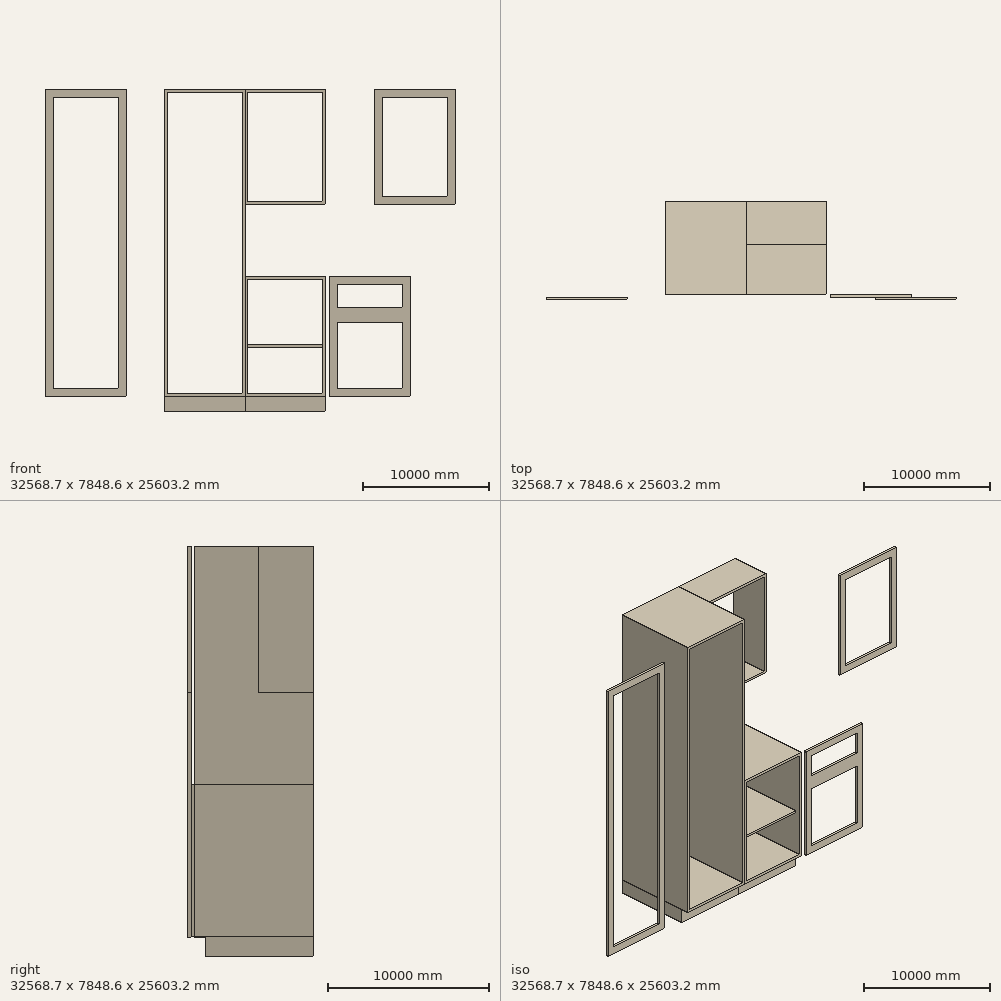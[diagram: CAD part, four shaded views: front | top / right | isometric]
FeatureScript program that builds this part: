
annotation { "Feature Type Name" : "Feature", "Feature Type Description" : "" }
export const myFeature = defineFeature(function(context is Context, id is Id, definition is map)
    precondition{}
    {
        {
            var Q0;
            Q0=qCreatedBy(makeId("Front.planeOp"),FACE);
            var sketch = newSketch(context, id + "F0", { "sketchPlane" : qUnion([Q0])});
            skLineSegment(sketch, "E0.bottom", {"start": v(0, 0) * mm, "end": v(6400.8, 0) * mm});
            skLineSegment(sketch, "E0.top", {"start": v(0, 24384) * mm, "end": v(6400.8, 24384) * mm});
            skLineSegment(sketch, "E0.left", {"start": v(0, 0) * mm, "end": v(0, 24384) * mm});
            skLineSegment(sketch, "E0.right", {"start": v(6400.8, 0) * mm, "end": v(6400.8, 24384) * mm});
            skSolve(sketch);
        }
        {
            var Q0;
            Q0=qCreatedBy(makeId("Front.planeOp"),FACE);
            var sketch = newSketch(context, id + "F1", { "sketchPlane" : qUnion([Q0])});
            skLineSegment(sketch, "E1.bottom", {"start": v(6400.8, 0) * mm, "end": v(12801.6, 0) * mm});
            skLineSegment(sketch, "E1.top", {"start": v(6400.8, 9525) * mm, "end": v(12801.6, 9525) * mm});
            skLineSegment(sketch, "E1.left", {"start": v(6400.8, 0) * mm, "end": v(6400.8, 9525) * mm});
            skLineSegment(sketch, "E1.right", {"start": v(12801.6, 0) * mm, "end": v(12801.6, 9525) * mm});
            skSolve(sketch);
        }
        {
            var Q0;
            Q0=qCreatedBy(makeId("Front.planeOp"),FACE);
            var sketch = newSketch(context, id + "F2", { "sketchPlane" : qUnion([Q0])});
            skLineSegment(sketch, "E2.bottom", {"start": v(6400.8, 24384) * mm, "end": v(12801.6, 24384) * mm});
            skLineSegment(sketch, "E2.top", {"start": v(6400.8, 15240) * mm, "end": v(12801.6, 15240) * mm});
            skLineSegment(sketch, "E2.left", {"start": v(6400.8, 24384) * mm, "end": v(6400.8, 15240) * mm});
            skLineSegment(sketch, "E2.right", {"start": v(12801.6, 24384) * mm, "end": v(12801.6, 15240) * mm});
            skSolve(sketch);
        }
        {
            var Q0;
            Q0=makeQuery(id+"F0.imprint","IMPRINT",FACE,{"disambiguationData":[TD([[makeQuery(id+"F0.imprint","IMPRINT",EDGE,{"derivedFrom":sQuery(id+"F0.wireOp",EDGE,"E0.bottom")}),1.0]])]});
            extrude(context, id + "F3", {"entities" : qUnion([Q0]), "depth" : 7391.4 * mm});
        }
        {
            var Q0;
            Q0=makeQuery(id+"F2.imprint","IMPRINT",FACE,{"disambiguationData":[TD([[makeQuery(id+"F2.imprint","IMPRINT",EDGE,{"derivedFrom":sQuery(id+"F2.wireOp",EDGE,"E2.bottom")}),-1.0]])]});
            extrude(context, id + "F4", {"entities" : qUnion([Q0]), "depth" : 3429 * mm});
        }
        {
            var Q0;
            Q0=makeQuery(id+"F1.imprint","IMPRINT",FACE,{"disambiguationData":[TD([[makeQuery(id+"F1.imprint","IMPRINT",EDGE,{"derivedFrom":sQuery(id+"F1.wireOp",EDGE,"E1.bottom")}),1.0]])]});
            extrude(context, id + "F5", {"entities" : qUnion([Q0]), "depth" : 7391.4 * mm});
        }
        {
            var Q0;
            Q0=qCreatedBy(makeId("Front.planeOp"),FACE);
            var sketch = newSketch(context, id + "F6", { "sketchPlane" : qUnion([Q0])});
            skLineSegment(sketch, "E3.bottom", {"start": v(0, 0) * mm, "end": v(6400.8, 0) * mm});
            skLineSegment(sketch, "E3.top", {"start": v(0, -1219.2) * mm, "end": v(6400.8, -1219.2) * mm});
            skLineSegment(sketch, "E3.left", {"start": v(0, 0) * mm, "end": v(0, -1219.2) * mm});
            skLineSegment(sketch, "E3.right", {"start": v(6400.8, 0) * mm, "end": v(6400.8, -1219.2) * mm});
            skSolve(sketch);
        }
        {
            var Q0;
            Q0=makeQuery(id+"F6.imprint","IMPRINT",FACE,{"disambiguationData":[TD([[makeQuery(id+"F6.imprint","IMPRINT",EDGE,{"derivedFrom":sQuery(id+"F6.wireOp",EDGE,"E3.bottom")}),-1.0]])]});
            var sketch = newSketch(context, id + "F7", { "sketchPlane" : qUnion([Q0])});
            skLineSegment(sketch, "E4.bottom", {"start": v(6400.8, -1219.2) * mm, "end": v(12801.6, -1219.2) * mm});
            skLineSegment(sketch, "E4.top", {"start": v(6400.8, 0) * mm, "end": v(12801.6, 0) * mm});
            skLineSegment(sketch, "E4.left", {"start": v(6400.8, -1219.2) * mm, "end": v(6400.8, 0) * mm});
            skLineSegment(sketch, "E4.right", {"start": v(12801.6, -1219.2) * mm, "end": v(12801.6, 0) * mm});
            skSolve(sketch);
        }
        {
            var Q0;
            Q0=makeQuery(id+"F6.imprint","IMPRINT",FACE,{"disambiguationData":[TD([[makeQuery(id+"F6.imprint","IMPRINT",EDGE,{"derivedFrom":sQuery(id+"F6.wireOp",EDGE,"E3.bottom")}),-1.0]])]});
            extrude(context, id + "F8", {"entities" : qUnion([Q0]), "depth" : 6705.6 * mm});
        }
        {
            var Q0;
            Q0=makeQuery(id+"F7.imprint","IMPRINT",FACE,{"disambiguationData":[TD([[makeQuery(id+"F7.imprint","IMPRINT",EDGE,{"derivedFrom":sQuery(id+"F7.wireOp",EDGE,"E4.bottom")}),1.0]])]});
            extrude(context, id + "F9", {"entities" : qUnion([Q0]), "depth" : 6705.6 * mm});
        }
        {
            var Q0;
            Q0=makeQuery(id+"F3.opExtrude","CAP_FACE",FACE,{"disambiguationData":[OSD([sQuery(id+"F0.wireOp",EDGE,"E0.bottom"),sQuery(id+"F0.wireOp",EDGE,"E0.top"),sQuery(id+"F0.wireOp",EDGE,"E0.left"),sQuery(id+"F0.wireOp",EDGE,"E0.right")])],"isStart":false});
            var sketch = newSketch(context, id + "F10", { "sketchPlane" : qUnion([Q0])});
            skLineSegment(sketch, "E5.bottom", {"start": v(609.6, 23774.4) * mm, "end": v(5791.2, 23774.4) * mm});
            skLineSegment(sketch, "E5.top", {"start": v(609.6, 609.6) * mm, "end": v(5791.2, 609.6) * mm});
            skLineSegment(sketch, "E5.left", {"start": v(609.6, 23774.4) * mm, "end": v(609.6, 609.6) * mm});
            skLineSegment(sketch, "E5.right", {"start": v(5791.2, 23774.4) * mm, "end": v(5791.2, 609.6) * mm});
            skSolve(sketch);
        }
        {
            var Q0;
            Q0=makeQuery(id+"F3.opExtrude","CAP_FACE",FACE,{"disambiguationData":[OSD([sQuery(id+"F0.wireOp",EDGE,"E0.bottom"),sQuery(id+"F0.wireOp",EDGE,"E0.top"),sQuery(id+"F0.wireOp",EDGE,"E0.left"),sQuery(id+"F0.wireOp",EDGE,"E0.right")])],"isStart":true});
            var sketch = newSketch(context, id + "F11", { "sketchPlane" : qUnion([Q0])});
            skLineSegment(sketch, "E6.bottom", {"start": v(-6172.2, 24155.4) * mm, "end": v(-228.6, 24155.4) * mm});
            skLineSegment(sketch, "E6.top", {"start": v(-6172.2, 228.6) * mm, "end": v(-228.6, 228.6) * mm});
            skLineSegment(sketch, "E6.left", {"start": v(-6172.2, 24155.4) * mm, "end": v(-6172.2, 228.6) * mm});
            skLineSegment(sketch, "E6.right", {"start": v(-228.6, 24155.4) * mm, "end": v(-228.6, 228.6) * mm});
            skSolve(sketch);
        }
        {
            var Q0;
            Q0=makeQuery(id+"F11.imprint","IMPRINT",FACE,{"disambiguationData":[TD([[makeQuery(id+"F11.imprint","IMPRINT",EDGE,{"derivedFrom":sQuery(id+"F11.wireOp",EDGE,"E6.bottom")}),-1.0]])]});
            extrude(context, id + "F12", {"entities" : qUnion([Q0]), "operationType" : NewBodyOperationType.REMOVE, "oppositeDirection" : true, "depth" : 7391.4 * mm});
        }
        {
            var Q0;
            Q0 = qSketchRegion(id + "F10", true);
            extrude(context, id + "F13", {"entities" : qUnion([Q0]), "operationType" : NewBodyOperationType.REMOVE, "depth" : 228.6 * mm});
        }
        {
            var Q0;
            Q0=makeQuery(id+"F3.opExtrude","CAP_FACE",FACE,{"disambiguationData":[OSD([sQuery(id+"F0.wireOp",EDGE,"E0.bottom"),sQuery(id+"F0.wireOp",EDGE,"E0.top"),sQuery(id+"F0.wireOp",EDGE,"E0.left"),sQuery(id+"F0.wireOp",EDGE,"E0.right")])],"isStart":false});
            var sketch = newSketch(context, id + "F14", { "sketchPlane" : qUnion([Q0])});
            skLineSegment(sketch, "E7.bottom", {"start": v(0, 0) * mm, "end": v(6400.8, 0) * mm});
            skLineSegment(sketch, "E7.top", {"start": v(0, 24384) * mm, "end": v(6400.8, 24384) * mm});
            skLineSegment(sketch, "E7.left", {"start": v(0, 0) * mm, "end": v(0, 24384) * mm});
            skLineSegment(sketch, "E7.right", {"start": v(6400.8, 0) * mm, "end": v(6400.8, 24384) * mm});
            skSolve(sketch);
        }
        {
            var Q0;
            Q0=makeQuery(id+"F4.opExtrude","CAP_FACE",FACE,{"disambiguationData":[OSD([sQuery(id+"F2.wireOp",EDGE,"E2.bottom"),sQuery(id+"F2.wireOp",EDGE,"E2.top"),sQuery(id+"F2.wireOp",EDGE,"E2.left"),sQuery(id+"F2.wireOp",EDGE,"E2.right")])],"isStart":true});
            var sketch = newSketch(context, id + "F15", { "sketchPlane" : qUnion([Q0])});
            skLineSegment(sketch, "E8.bottom", {"start": v(-12573, 24155.4) * mm, "end": v(-6629.4, 24155.4) * mm});
            skLineSegment(sketch, "E8.top", {"start": v(-12573, 15468.6) * mm, "end": v(-6629.4, 15468.6) * mm});
            skLineSegment(sketch, "E8.left", {"start": v(-12573, 24155.4) * mm, "end": v(-12573, 15468.6) * mm});
            skLineSegment(sketch, "E8.right", {"start": v(-6629.4, 24155.4) * mm, "end": v(-6629.4, 15468.6) * mm});
            skSolve(sketch);
        }
        {
            var Q0;
            Q0=makeQuery(id+"F15.imprint","IMPRINT",FACE,{"disambiguationData":[TD([[makeQuery(id+"F15.imprint","IMPRINT",EDGE,{"derivedFrom":sQuery(id+"F15.wireOp",EDGE,"E8.bottom")}),-1.0]])]});
            extrude(context, id + "F16", {"entities" : qUnion([Q0]), "operationType" : NewBodyOperationType.REMOVE, "oppositeDirection" : true, "depth" : 3429 * mm});
        }
        {
            var Q0;
            Q0=makeQuery(id+"F5.opExtrude","CAP_FACE",FACE,{"disambiguationData":[OSD([sQuery(id+"F1.wireOp",EDGE,"E1.bottom"),sQuery(id+"F1.wireOp",EDGE,"E1.top"),sQuery(id+"F1.wireOp",EDGE,"E1.left"),sQuery(id+"F1.wireOp",EDGE,"E1.right")])],"isStart":true});
            var sketch = newSketch(context, id + "F17", { "sketchPlane" : qUnion([Q0])});
            skLineSegment(sketch, "E9.bottom", {"start": v(-12573, 228.6) * mm, "end": v(-6629.4, 228.6) * mm});
            skLineSegment(sketch, "E9.top", {"start": v(-12573, 9296.4) * mm, "end": v(-6629.4, 9296.4) * mm});
            skLineSegment(sketch, "E9.left", {"start": v(-12573, 228.6) * mm, "end": v(-12573, 9296.4) * mm});
            skLineSegment(sketch, "E9.right", {"start": v(-6629.4, 228.6) * mm, "end": v(-6629.4, 9296.4) * mm});
            skSolve(sketch);
        }
        {
            var Q0;
            Q0=makeQuery(id+"F17.imprint","IMPRINT",FACE,{"disambiguationData":[TD([[makeQuery(id+"F17.imprint","IMPRINT",EDGE,{"derivedFrom":sQuery(id+"F17.wireOp",EDGE,"E9.bottom")}),1.0]])]});
            extrude(context, id + "F18", {"entities" : qUnion([Q0]), "operationType" : NewBodyOperationType.REMOVE, "oppositeDirection" : true, "depth" : 7391.4 * mm});
        }
        {
            var Q0;
            Q0=makeQuery(id+"F5.opExtrude","CAP_FACE",FACE,{"disambiguationData":[OSD([sQuery(id+"F1.wireOp",EDGE,"E1.bottom"),sQuery(id+"F1.wireOp",EDGE,"E1.top"),sQuery(id+"F1.wireOp",EDGE,"E1.left"),sQuery(id+"F1.wireOp",EDGE,"E1.right")])],"isStart":false});
            var sketch = newSketch(context, id + "F19", { "sketchPlane" : qUnion([Q0])});
            skLineSegment(sketch, "E10.bottom", {"start": v(13107.73, 9525) * mm, "end": v(19508.53, 9525) * mm});
            skLineSegment(sketch, "E10.top", {"start": v(13107.73, 0) * mm, "end": v(19508.53, 0) * mm});
            skLineSegment(sketch, "E10.left", {"start": v(13107.73, 9525) * mm, "end": v(13107.73, 0) * mm});
            skLineSegment(sketch, "E10.right", {"start": v(19508.53, 9525) * mm, "end": v(19508.53, 0) * mm});
            skLineSegment(sketch, "E11.bottom", {"start": v(13717.33, 8915.4) * mm, "end": v(18898.93, 8915.4) * mm});
            skLineSegment(sketch, "E11.top", {"start": v(13717.33, 7086.6) * mm, "end": v(18898.93, 7086.6) * mm});
            skLineSegment(sketch, "E11.left", {"start": v(13717.33, 8915.4) * mm, "end": v(13717.33, 7086.6) * mm});
            skLineSegment(sketch, "E11.right", {"start": v(18898.93, 8915.4) * mm, "end": v(18898.93, 7086.6) * mm});
            skLineSegment(sketch, "E12.bottom", {"start": v(13717.33, 5867.4) * mm, "end": v(18898.93, 5867.4) * mm});
            skLineSegment(sketch, "E12.top", {"start": v(13717.33, 609.6) * mm, "end": v(18898.93, 609.6) * mm});
            skLineSegment(sketch, "E12.left", {"start": v(13717.33, 5867.4) * mm, "end": v(13717.33, 609.6) * mm});
            skLineSegment(sketch, "E12.right", {"start": v(18898.93, 5867.4) * mm, "end": v(18898.93, 609.6) * mm});
            skSolve(sketch);
        }
        {
            var Q0;
            Q0=makeQuery(id+"F19.imprint","IMPRINT",FACE,{"disambiguationData":[TD([[makeQuery(id+"F19.imprint","IMPRINT",EDGE,{"derivedFrom":sQuery(id+"F19.wireOp",EDGE,"E10.bottom")}),-1.0]])]});
            extrude(context, id + "F20", {"entities" : qUnion([Q0]), "depth" : 228.6 * mm});
        }
        {
            var Q0;
            Q0=makeQuery(id+"F18.boolean.opBoolean","COPY",FACE,{"derivedFrom":makeQuery(id+"F18.opExtrude","SWEPT_FACE",FACE,{"disambiguationData":[OSD([sQuery(id+"F17.wireOp",EDGE,"E9.bottom")])]})});
            var sketch = newSketch(context, id + "F21", { "sketchPlane" : qUnion([Q0])});
            skLineSegment(sketch, "E13.bottom", {"start": v(6629.4, 0) * mm, "end": v(12573, 0) * mm});
            skLineSegment(sketch, "E13.top", {"start": v(6629.4, -7010.4) * mm, "end": v(12573, -7010.4) * mm});
            skLineSegment(sketch, "E13.left", {"start": v(6629.4, 0) * mm, "end": v(6629.4, -7010.4) * mm});
            skLineSegment(sketch, "E13.right", {"start": v(12573, 0) * mm, "end": v(12573, -7010.4) * mm});
            skSolve(sketch);
        }
        {
            var Q0;
            Q0=makeQuery(id+"F21.imprint","IMPRINT",FACE,{"disambiguationData":[TD([[makeQuery(id+"F21.imprint","IMPRINT",EDGE,{"derivedFrom":sQuery(id+"F21.wireOp",EDGE,"E13.bottom")}),1.0]])]});
            extrude(context, id + "F22", {"entities" : qUnion([Q0]), "depth" : 228.6 * mm});
        }
        {
            var Q0;
            Q0=makeQuery(id+"F22.opExtrude","SWEPT_BODY",BODY,{"disambiguationData":[OSD([sQuery(id+"F21.wireOp",EDGE,"E13.bottom"),sQuery(id+"F21.wireOp",EDGE,"E13.top"),sQuery(id+"F21.wireOp",EDGE,"E13.left"),sQuery(id+"F21.wireOp",EDGE,"E13.right")])]});
            transform(context, id + "F23", {"entities" : qUnion([Q0]), "transformType" : TransformType.TRANSLATION_3D, "dx" : 0 * mm, "dy" : 0 * mm, "dz" : 3657.6 * mm, "makeCopy" : false});
        }
        {
            var Q0;
            Q0=qCreatedBy(makeId("Front.planeOp"),FACE);
            var sketch = newSketch(context, id + "F24", { "sketchPlane" : qUnion([Q0])});
            skLineSegment(sketch, "E14", {"start": v(0, 0) * mm, "end": v(-3048, 0) * mm});
            skLineSegment(sketch, "E15.bottom", {"start": v(-3048, 0) * mm, "end": v(-9448.8, 0) * mm});
            skLineSegment(sketch, "E15.top", {"start": v(-3048, 24384) * mm, "end": v(-9448.8, 24384) * mm});
            skLineSegment(sketch, "E15.left", {"start": v(-3048, 0) * mm, "end": v(-3048, 24384) * mm});
            skLineSegment(sketch, "E15.right", {"start": v(-9448.8, 0) * mm, "end": v(-9448.8, 24384) * mm});
            skLineSegment(sketch, "E16.bottom", {"start": v(-8839.2, 23774.4) * mm, "end": v(-3657.6, 23774.4) * mm});
            skLineSegment(sketch, "E16.top", {"start": v(-8839.2, 609.6) * mm, "end": v(-3657.6, 609.6) * mm});
            skLineSegment(sketch, "E16.left", {"start": v(-8839.2, 23774.4) * mm, "end": v(-8839.2, 609.6) * mm});
            skLineSegment(sketch, "E16.right", {"start": v(-3657.6, 23774.4) * mm, "end": v(-3657.6, 609.6) * mm});
            skSolve(sketch);
        }
        {
            var Q0;
            Q0=makeQuery(id+"F24.imprint","IMPRINT",FACE,{"disambiguationData":[TD([[makeQuery(id+"F24.imprint","IMPRINT",EDGE,{"derivedFrom":sQuery(id+"F24.wireOp",EDGE,"E15.bottom")}),-1.0]])]});
            extrude(context, id + "F25", {"entities" : qUnion([Q0]), "depth" : 228.6 * mm});
        }
        {
            var Q0;
            Q0=makeQuery(id+"F25.opExtrude","SWEPT_BODY",BODY,{"disambiguationData":[OSD([sQuery(id+"F24.wireOp",EDGE,"E15.bottom"),sQuery(id+"F24.wireOp",EDGE,"E15.top"),sQuery(id+"F24.wireOp",EDGE,"E15.left"),sQuery(id+"F24.wireOp",EDGE,"E15.right"),sQuery(id+"F24.wireOp",EDGE,"E16.bottom"),sQuery(id+"F24.wireOp",EDGE,"E16.top"),sQuery(id+"F24.wireOp",EDGE,"E16.left"),sQuery(id+"F24.wireOp",EDGE,"E16.right")])]});
            transform(context, id + "F26", {"entities" : qUnion([Q0]), "transformType" : TransformType.TRANSLATION_3D, "dx" : 0 * mm, "dy" : -7620 * mm, "dz" : 0 * mm, "makeCopy" : false});
        }
        {
            var Q0;
            Q0=qCreatedBy(makeId("Front.planeOp"),FACE);
            var sketch = newSketch(context, id + "F27", { "sketchPlane" : qUnion([Q0])});
            skLineSegment(sketch, "E17.bottom", {"start": v(16719.14, 15236.86) * mm, "end": v(23119.94, 15236.86) * mm});
            skLineSegment(sketch, "E17.top", {"start": v(16719.14, 24380.86) * mm, "end": v(23119.94, 24380.86) * mm});
            skLineSegment(sketch, "E17.left", {"start": v(16719.14, 15236.86) * mm, "end": v(16719.14, 24380.86) * mm});
            skLineSegment(sketch, "E17.right", {"start": v(23119.94, 15236.86) * mm, "end": v(23119.94, 24380.86) * mm});
            skLineSegment(sketch, "E18.bottom", {"start": v(17328.74, 23771.26) * mm, "end": v(22510.34, 23771.26) * mm});
            skLineSegment(sketch, "E18.top", {"start": v(17328.74, 15846.46) * mm, "end": v(22510.34, 15846.46) * mm});
            skLineSegment(sketch, "E18.left", {"start": v(17328.74, 23771.26) * mm, "end": v(17328.74, 15846.46) * mm});
            skLineSegment(sketch, "E18.right", {"start": v(22510.34, 23771.26) * mm, "end": v(22510.34, 15846.46) * mm});
            skSolve(sketch);
        }
        {
            var Q0;
            Q0=makeQuery(id+"F27.imprint","IMPRINT",FACE,{"disambiguationData":[TD([[makeQuery(id+"F27.imprint","IMPRINT",EDGE,{"derivedFrom":sQuery(id+"F27.wireOp",EDGE,"E17.bottom")}),1.0]])]});
            extrude(context, id + "F28", {"entities" : qUnion([Q0]), "depth" : 228.6 * mm});
        }
        {
            var Q0;
            Q0=makeQuery(id+"F28.opExtrude","SWEPT_BODY",BODY,{"disambiguationData":[OSD([sQuery(id+"F27.wireOp",EDGE,"E17.bottom"),sQuery(id+"F27.wireOp",EDGE,"E17.top"),sQuery(id+"F27.wireOp",EDGE,"E17.left"),sQuery(id+"F27.wireOp",EDGE,"E17.right"),sQuery(id+"F27.wireOp",EDGE,"E18.bottom"),sQuery(id+"F27.wireOp",EDGE,"E18.top"),sQuery(id+"F27.wireOp",EDGE,"E18.left"),sQuery(id+"F27.wireOp",EDGE,"E18.right")])]});
            transform(context, id + "F29", {"entities" : qUnion([Q0]), "transformType" : TransformType.TRANSLATION_3D, "dx" : 0 * mm, "dy" : -7620 * mm, "dz" : 0 * mm, "makeCopy" : false});
        }
    });
